FREECAD ASSEMBLY — COMPONENT RECIPES ("CWSensorKey-Assembly")

This assembly document has 6 components, labeled P0..P5 below (a component is one placed body or linked part). 0 of them carry a construction recipe — the FreeCAD feature program that regenerates the part from scratch, quoted from this document or its linked companion documents; the rest are supplied as boundary geometry only. No exploded tour is included for this assembly.
COMPONENT P0 — geometry summary ("Body"; no construction recipe available for this part):
  bounding box: 43.0 x 22.0 x 2.0 mm
  tessellated surface: 1,076 triangles
  volume: 1684 mm^3 (89% of its bounding box)
  symmetry: 2-fold rotationally symmetric about the z axis; mirror-symmetric across its x mid-plane, y mid-plane
COMPONENT P1 — geometry summary ("Body001"; no construction recipe available for this part):
  bounding box: 43.0 x 22.0 x 2.0 mm
  tessellated surface: 1,076 triangles
  volume: 1684 mm^3 (89% of its bounding box)
  symmetry: 2-fold rotationally symmetric about the z axis; mirror-symmetric across its x mid-plane, y mid-plane
COMPONENT P2 — geometry summary ("CW-Pad-Middle-Dah"; no construction recipe available for this part):
  bounding box: 36.0 x 24.0 x 2.0 mm
  tessellated surface: 724 triangles
  volume: 1477 mm^3 (85% of its bounding box)
COMPONENT P3 — geometry summary ("CW-Pad-Middle-Dit"; no construction recipe available for this part):
  bounding box: 36.0 x 24.0 x 2.0 mm
  tessellated surface: 724 triangles
  volume: 1477 mm^3 (85% of its bounding box)
COMPONENT P4 — geometry summary ("CW-Pad-Side"; no construction recipe available for this part):
  bounding box: 28.5 x 24.0 x 2.0 mm
  tessellated surface: 768 triangles
  volume: 632 mm^3 (46% of its bounding box)
  symmetry: mirror-symmetric across its y mid-plane, z mid-plane
COMPONENT P5 — geometry summary ("CW-Pad-Side001"; no construction recipe available for this part):
  bounding box: 28.5 x 24.0 x 2.0 mm
  tessellated surface: 768 triangles
  volume: 632 mm^3 (46% of its bounding box)
  symmetry: mirror-symmetric across its y mid-plane, z mid-plane
PROVENANCE & LICENSES
A FreeCAD (.FCStd) document from a public repository crawl; recipes are the document's own serialized feature recipes (and, for linked parts, companion documents' recipes).
License: as declared in the source repository (recorded in the dataset sidecar).
